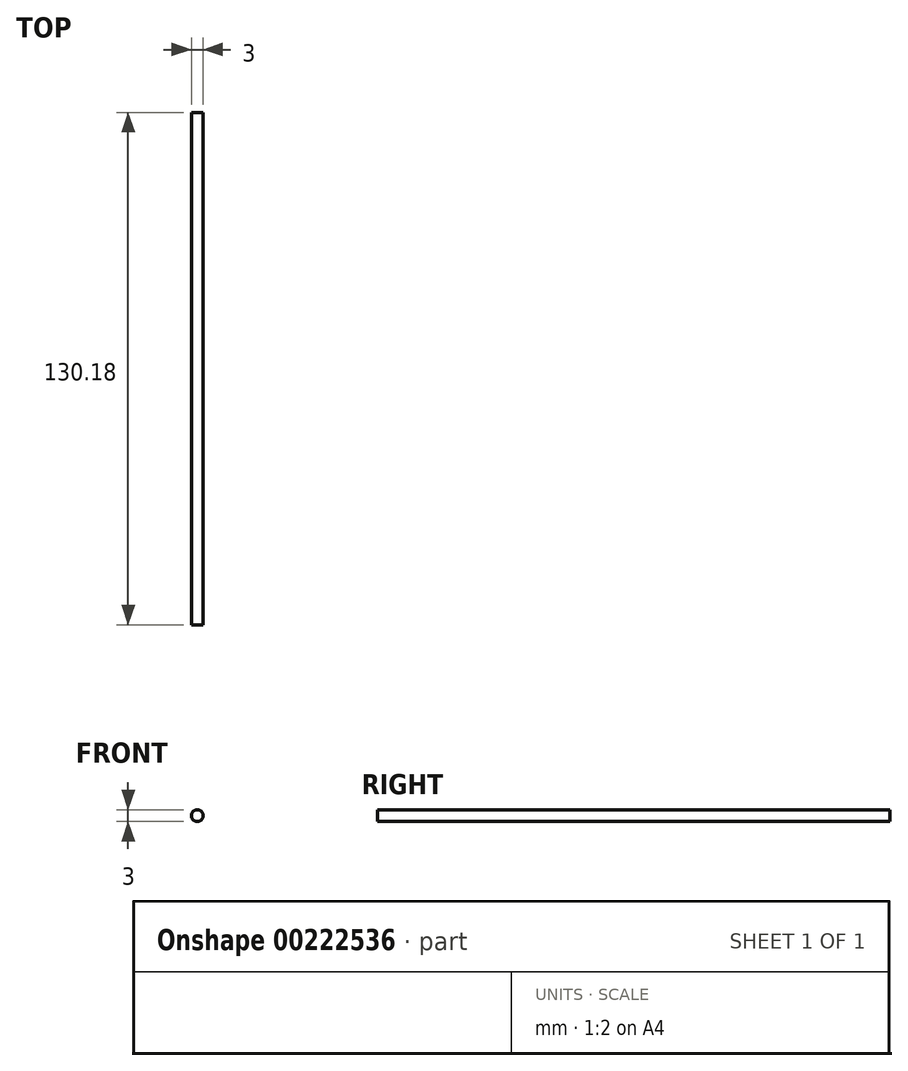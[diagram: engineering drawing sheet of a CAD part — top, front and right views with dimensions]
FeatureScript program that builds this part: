
annotation { "Feature Type Name" : "Feature", "Feature Type Description" : "" }
export const myFeature = defineFeature(function(context is Context, id is Id, definition is map)
    precondition{}
    {
        {
            var Q0;
            Q0=qCreatedBy(makeId("Front.planeOp"),FACE);
            var sketch = newSketch(context, id + "F0", { "sketchPlane" : qUnion([Q0])});
            skCircle(sketch, "E0", {"center": v(0, 0) * mm, "radius": 1.5 * mm});
            skSolve(sketch);
        }
        {
            var Q0;
            Q0 = qSketchRegion(id + "F0", true);
            extrude(context, id + "F1", {"entities" : qUnion([Q0]), "depth" : 130.17 * mm});
        }
    });
